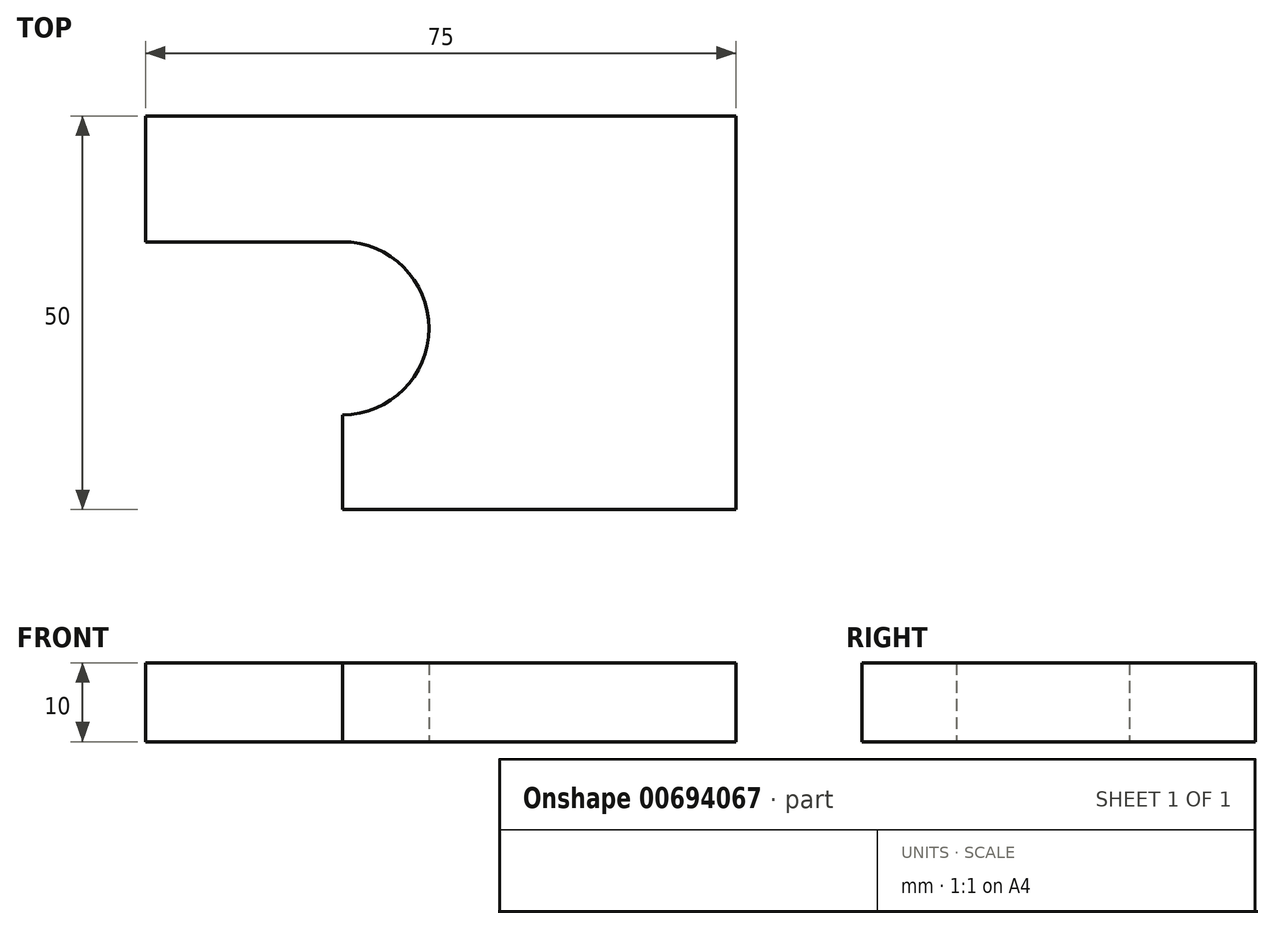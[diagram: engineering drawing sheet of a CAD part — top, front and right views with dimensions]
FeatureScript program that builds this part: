
annotation { "Feature Type Name" : "Feature", "Feature Type Description" : "" }
export const myFeature = defineFeature(function(context is Context, id is Id, definition is map)
    precondition{}
    {
        {
            var Q0;
            Q0=qCreatedBy(makeId("Top.planeOp"), FACE);
            var sketch = newSketch(context, id + "F0", { "sketchPlane" : qUnion([Q0])});
            skLineSegment(sketch, "E0.bottom", {"start": v(28.63, 0) * mm, "end": v(78.63, 0) * mm});
            skLineSegment(sketch, "E0.top", {"start": v(3.63, 50) * mm, "end": v(78.63, 50) * mm});
            skLineSegment(sketch, "E0.left", {"start": v(3.63, 34) * mm, "end": v(3.63, 50) * mm});
            skLineSegment(sketch, "E0.right", {"start": v(78.63, 0) * mm, "end": v(78.63, 50) * mm});
            skLineSegment(sketch, "E1", {"start": v(3.63, 34) * mm, "end": v(28.63, 34) * mm});
            skLineSegment(sketch, "E2", {"start": v(28.63, 12) * mm, "end": v(28.63, 0) * mm});
            skArc(sketch, "E3", {"start": v(28.63, 12) * mm, "mid": v(39.63, 23) * mm, "end": v(28.63, 34) * mm});
            skSolve(sketch);
        }
        {
            var Q0;
            Q0 = qSketchRegion(id + "F0", true);
            extrude(context, id + "F1", {"entities" : qUnion([Q0]), "depth" : 10 * mm, "offsetDistance" : 25 * mm});
        }
    });
